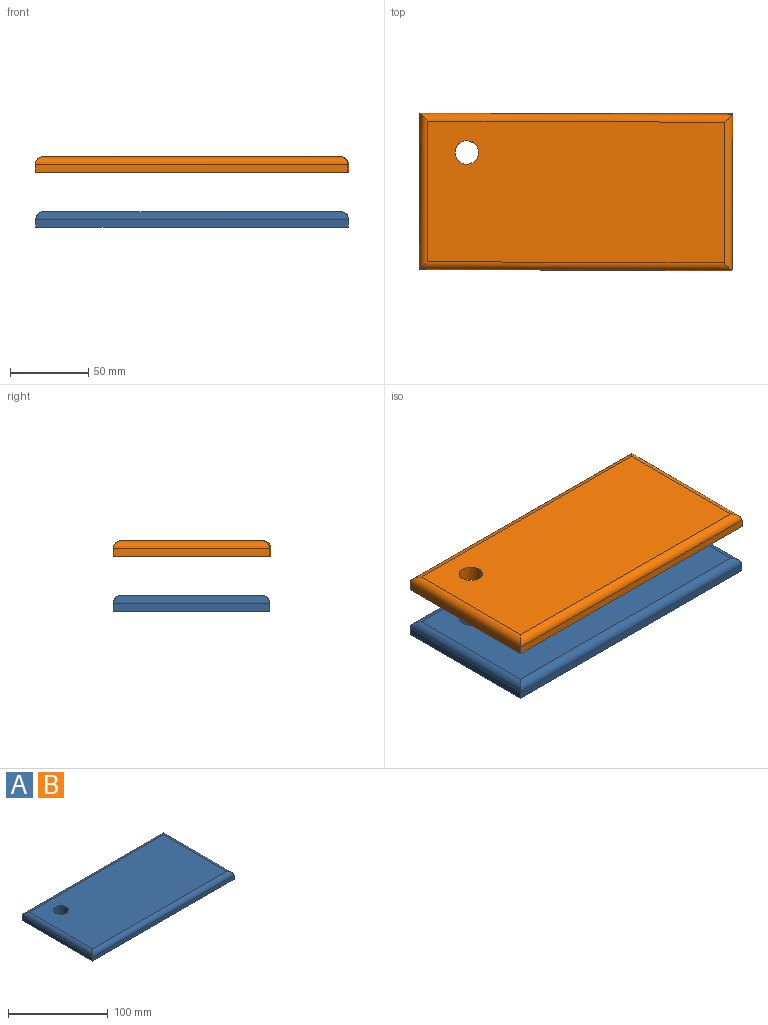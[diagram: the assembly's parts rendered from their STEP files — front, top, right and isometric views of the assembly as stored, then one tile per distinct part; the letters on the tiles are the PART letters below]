
ASSEMBLY  parts=2 mates=2
PART A: 11 faces, bbox 200x100x10 mm
  f0: plane 200x5mm, normal (0,1,0), area 1000mm2, adj f1,f3,f5,f6
  f1: plane 100x5mm, normal (-1,0,0), area 500mm2, adj f0,f2,f5,f7
  f2: plane 200x5mm, normal (0,-1,0), area 1000mm2, adj f1,f3,f5,f9
  f3: plane 100x5mm, normal (1,0,0), area 500mm2, adj f0,f2,f5,f8
  f4: plane 190x90mm, normal (0,0,1), area 16923.3mm2, adj f6,f7,f8,f9,f10
  f5: plane 200x100mm, normal (0,0,-1), area 19823.3mm2, adj f0,f1,f2,f3,f10
  f6: cylinder r=5mm len=200mm, axis (1,0,0), area 1542.3mm2, adj f0,f4,f7,f8
  f7: cylinder r=5mm len=100mm, axis (0,1,0), area 756.9mm2, adj f1,f4,f6,f9
  f8: cylinder r=5mm len=100mm, axis (0,-1,0), area 756.9mm2, adj f3,f4,f6,f9
  f9: cylinder r=5mm len=200mm, axis (-1,0,0), area 1542.3mm2, adj f2,f4,f7,f8
  f10: cylinder r=7.5mm len=15mm, axis (0,0,1), area 471.2mm2, adj f4,f5
PART B: same geometry as A
PLACE A t=(-29.05,-3.85,39.68)mm fixed
PLACE B rot(axis=(0,0,-1),0.2deg) t=(-29.36,-3.73,74.68)mm
MATE parallel B.f4 <-> A.f5  axis (0,0,1) through (71.58,45.59,84.68)mm
MATE cylindrical A.f10 <-> B.f10  axis (0,0,1) through (0.95,71.15,44.68)mm
